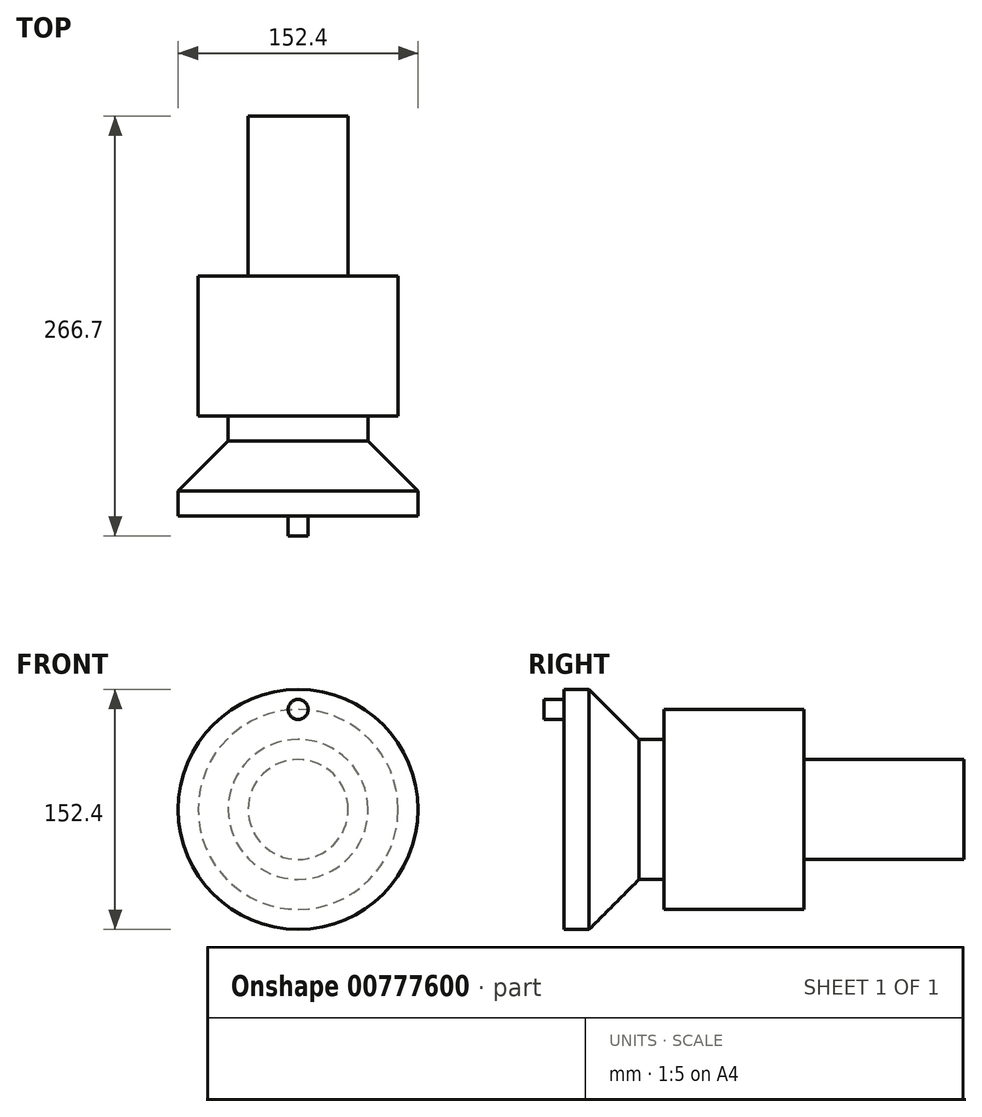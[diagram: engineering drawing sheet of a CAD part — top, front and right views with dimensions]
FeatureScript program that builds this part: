
annotation { "Feature Type Name" : "Feature", "Feature Type Description" : "" }
export const myFeature = defineFeature(function(context is Context, id is Id, definition is map)
    precondition{}
    {
        {
            var Q0;
            Q0=qCreatedBy(makeId("Right.planeOp"),FACE);
            var sketch = newSketch(context, id + "F0", { "sketchPlane" : qUnion([Q0])});
            skLineSegment(sketch, "E0", {"start": v(0, 0) * mm, "end": v(0, 31.75) * mm});
            skLineSegment(sketch, "E1", {"start": v(0, 31.75) * mm, "end": v(-101.6, 31.75) * mm});
            skLineSegment(sketch, "E2", {"start": v(-101.6, 31.75) * mm, "end": v(-101.6, 63.5) * mm});
            skLineSegment(sketch, "E3", {"start": v(-101.6, 63.5) * mm, "end": v(-190.5, 63.5) * mm});
            skLineSegment(sketch, "E4", {"start": v(-190.5, 63.5) * mm, "end": v(-190.5, 44.45) * mm});
            skLineSegment(sketch, "E5", {"start": v(-190.5, 44.45) * mm, "end": v(-206.38, 44.45) * mm});
            skLineSegment(sketch, "E6", {"start": v(-206.38, 44.45) * mm, "end": v(-238.12, 76.2) * mm});
            skLineSegment(sketch, "E7", {"start": v(-254, 76.2) * mm, "end": v(-254, 0) * mm});
            skLineSegment(sketch, "E8", {"start": v(-254, 0) * mm, "end": v(0, 0) * mm});
            skLineSegment(sketch, "E9", {"start": v(-238.12, 76.2) * mm, "end": v(-254, 76.2) * mm});
            skSolve(sketch);
        }
        {
            var Q0;
            Q0 = qSketchRegion(id + "F0", true);
            var Q1;
            Q1=sQuery(id+"F0.wireOp",EDGE,"E8");
            revolve(context, id + "F1", {"surfaceOperationType" : NewSurfaceOperationType.NEW, "entities" : qUnion([Q0]), "axis" : qUnion([Q1]), "revolveType" : RevolveType.FULL});
        }
        {
            var Q0;
            Q0=makeQuery(id+"F1.opRevolve","SWEPT_FACE",FACE,{"disambiguationData":[OSD([sQuery(id+"F0.wireOp",EDGE,"E7")])]});
            var sketch = newSketch(context, id + "F2", { "sketchPlane" : qUnion([Q0])});
            skCircle(sketch, "E10", {"center": v(0, 63.5) * mm, "radius": 6.35 * mm});
            skSolve(sketch);
        }
        {
            var Q0;
            Q0 = qSketchRegion(id + "F2", true);
            extrude(context, id + "F3", {"entities" : qUnion([Q0]), "operationType" : NewBodyOperationType.ADD, "depth" : 12.7 * mm, "offsetDistance" : 25.4 * mm});
        }
    });
